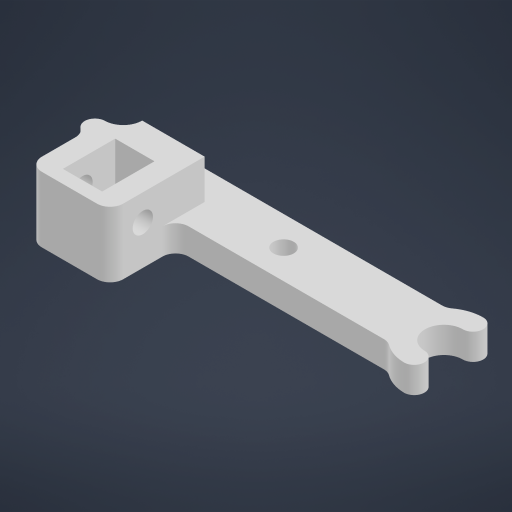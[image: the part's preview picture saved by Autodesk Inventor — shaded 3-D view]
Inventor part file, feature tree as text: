
AUTODESK INVENTOR PART (.ipt)
format: ipt  version: 2023 (Build 270158000, 158)  size: 263,680 bytes
history: native  units: mm
features: sketch x3, extrude x3, fillet x1
ambient origin geometry x8: Origin, YZ Plane, XZ Plane, XY Plane, X Axis, Y Axis, Z Axis, Center Point
bodies: Solid1 (feature_tree)
feature tree (7):
  sketch  "Sketch1"  dims[d0=20.0mm d2=49.0mm d3=10.0mm d5=10.0mm d7=12.0mm]
  sketch  "Sketch2"  dims[d9=3.1mm d10=4.0mm d11=0.0mm]
  extrude  "Extrusion1"  Depth=10.0mm
  extrude  "Extrusion3"  Depth=4.0mm TaperAngle=0.0deg
  extrude  "Extrusion4"  Depth=10.0mm
  fillet  "Fillet1"  Radius=6.212mm
  sketch  "Sketch4"  dims[d14=12.424mm d15=10.0mm d16=6.212mm d22=10.0mm d23=0.0mm d24=3.0mm d25=8.0mm d26=8.0mm d27=3.1mm d28=4.0mm d29=10.0mm d30=0.0mm d31=3.0mm d32=2.0mm d17=0.872665mm]
